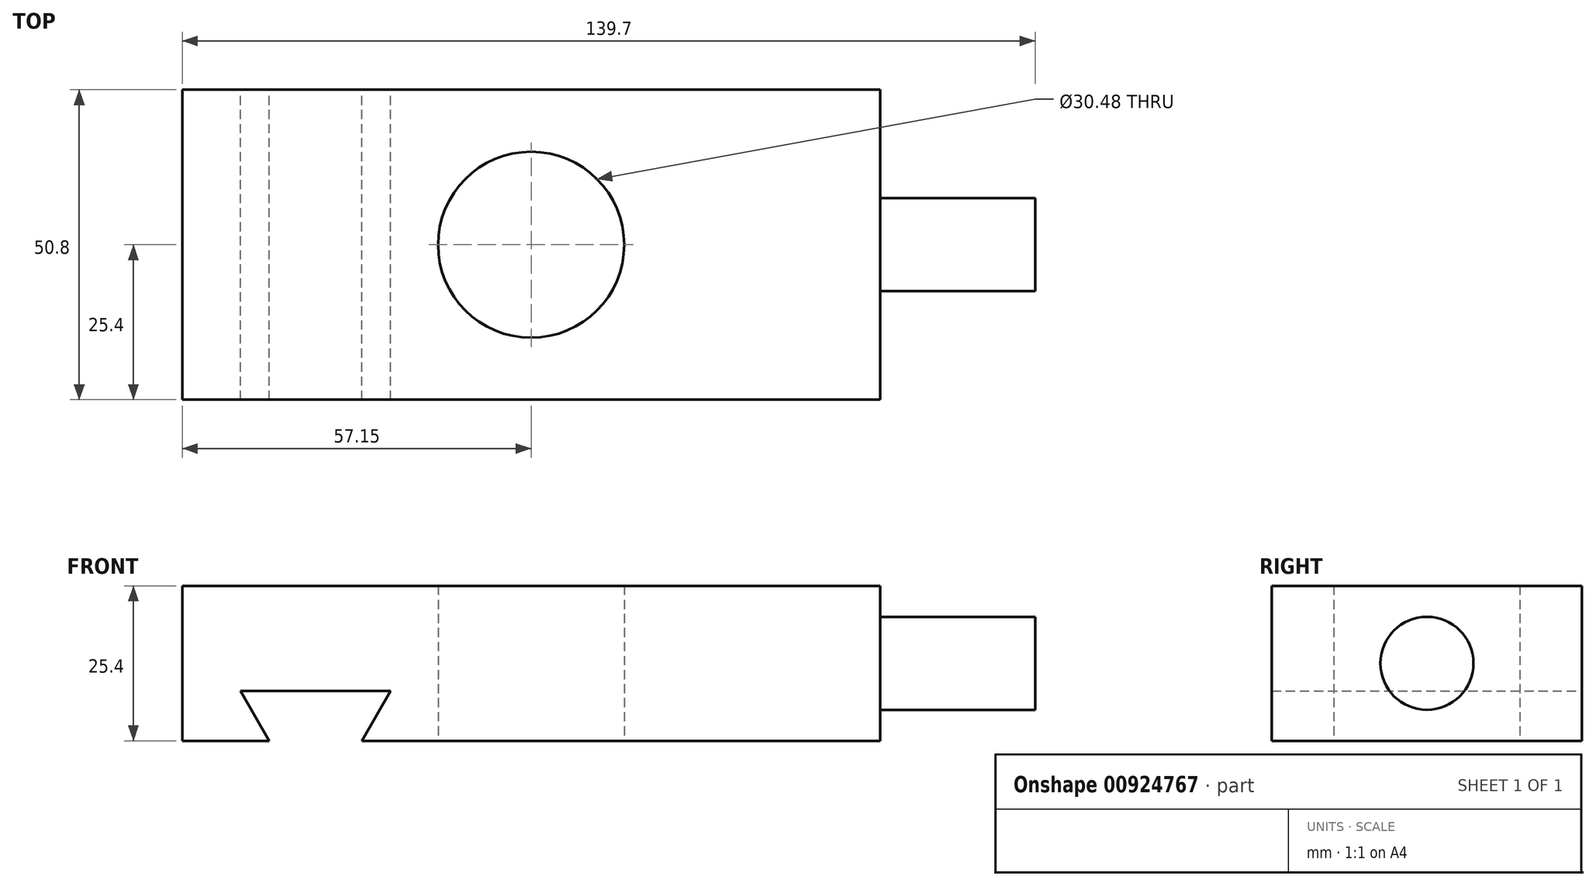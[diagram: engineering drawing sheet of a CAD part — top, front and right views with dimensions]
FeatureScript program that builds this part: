
annotation { "Feature Type Name" : "Feature", "Feature Type Description" : "" }
export const myFeature = defineFeature(function(context is Context, id is Id, definition is map)
    precondition{}
    {
        {
            var Q0;
            Q0=qCreatedBy(makeId("Top.planeOp"),FACE);
            var sketch = newSketch(context, id + "F0", { "sketchPlane" : qUnion([Q0])});
            skLineSegment(sketch, "E0.bottom", {"start": v(57.15, -25.4) * mm, "end": v(-57.15, -25.4) * mm});
            skLineSegment(sketch, "E0.top", {"start": v(57.15, 25.4) * mm, "end": v(-57.15, 25.4) * mm});
            skLineSegment(sketch, "E0.left", {"start": v(57.15, -25.4) * mm, "end": v(57.15, 25.4) * mm});
            skLineSegment(sketch, "E0.right", {"start": v(-57.15, -25.4) * mm, "end": v(-57.15, 25.4) * mm});
            skPoint(sketch, "E0.middle", {"position": v(0, 0) * mm});
            skCircle(sketch, "E1", {"center": v(0, 0) * mm, "radius": 15.24 * mm});
            skSolve(sketch);
        }
        {
            var Q0;
            Q0=makeQuery(id+"F0.imprint","IMPRINT",FACE,{"disambiguationData":[TD([[makeQuery(id+"F0.imprint","IMPRINT",EDGE,{"derivedFrom":sQuery(id+"F0.wireOp",EDGE,"E0.bottom")}),-1.0]])]});
            extrude(context, id + "F1", {"entities" : qUnion([Q0]), "depth" : 25.4 * mm, "offsetDistance" : 25.4 * mm});
        }
        {
            var Q0;
            Q0=makeQuery(id+"F1.opExtrude","CAP_FACE",FACE,{"disambiguationData":[OSD([sQuery(id+"F0.wireOp",EDGE,"E0.bottom"),sQuery(id+"F0.wireOp",EDGE,"E0.top"),sQuery(id+"F0.wireOp",EDGE,"E0.left"),sQuery(id+"F0.wireOp",EDGE,"E0.right"),sQuery(id+"F0.wireOp",EDGE,"E1")])],"isStart":false});
            var sketch = newSketch(context, id + "F2", { "sketchPlane" : qUnion([Q0])});
            skLineSegment(sketch, "E2.bottom", {"start": v(-42.93, 25.4) * mm, "end": v(-30.23, 25.4) * mm});
            skLineSegment(sketch, "E2.top", {"start": v(-42.93, -25.4) * mm, "end": v(-30.23, -25.4) * mm});
            skLineSegment(sketch, "E2.left", {"start": v(-42.93, 25.4) * mm, "end": v(-42.93, -25.4) * mm});
            skLineSegment(sketch, "E2.right", {"start": v(-30.23, 25.4) * mm, "end": v(-30.23, -25.4) * mm});
            skLineSegment(sketch, "E3.bottom", {"start": v(30.23, 25.4) * mm, "end": v(42.93, 25.4) * mm});
            skLineSegment(sketch, "E3.top", {"start": v(30.23, -25.4) * mm, "end": v(42.93, -25.4) * mm});
            skLineSegment(sketch, "E3.left", {"start": v(30.23, 25.4) * mm, "end": v(30.23, -25.4) * mm});
            skLineSegment(sketch, "E3.right", {"start": v(42.93, 25.4) * mm, "end": v(42.93, -25.4) * mm});
            skLineSegment(sketch, "E4", {"start": v(-25.15, 25.4) * mm, "end": v(-25.15, -25.4) * mm});
            skLineSegment(sketch, "E5", {"start": v(-17.53, 25.4) * mm, "end": v(-17.53, -25.4) * mm});
            skLineSegment(sketch, "E6", {"start": v(17.53, 25.4) * mm, "end": v(17.53, -25.4) * mm});
            skLineSegment(sketch, "E7", {"start": v(25.15, 25.4) * mm, "end": v(25.15, -25.4) * mm});
            skLineSegment(sketch, "E8", {"start": v(-3.81, 25.4) * mm, "end": v(-3.8, -25.4) * mm});
            skPoint(sketch, "E8.endSnap0", {"position": v(0, -25.4) * mm});
            skLineSegment(sketch, "E9", {"start": v(3.8, 25.4) * mm, "end": v(3.81, -25.4) * mm});
            skSolve(sketch);
        }
        {
            var Q0;
            Q0=makeQuery(id+"F1.opExtrude","SWEPT_FACE",FACE,{"disambiguationData":[OSD([sQuery(id+"F0.wireOp",EDGE,"E0.top")])]});
            var sketch = newSketch(context, id + "F3", { "sketchPlane" : qUnion([Q0])});
            skLineSegment(sketch, "E10", {"start": v(42.9, 0) * mm, "end": v(47.62, 8.17) * mm});
            skLineSegment(sketch, "E11", {"start": v(48.64, 8.17) * mm, "end": v(23.02, 8.17) * mm});
            skLineSegment(sketch, "E12", {"start": v(23.02, 8.17) * mm, "end": v(27.74, 0) * mm});
            skLineSegment(sketch, "E13", {"start": v(27.74, 0) * mm, "end": v(42.9, 0) * mm});
            skSolve(sketch);
        }
        {
            var Q0;
            {var subQ0=sQuery(id+"F3.wireOp",EDGE,"E10");Q0=makeQuery(id+"F3.imprint","IMPRINT",FACE,{"disambiguationData":[TD([[makeQuery(id+"F3.imprint","IMPRINT",EDGE,{"derivedFrom":subQ0}),1.0]])]});}
            extrude(context, id + "F4", {"entities" : qUnion([Q0]), "operationType" : NewBodyOperationType.REMOVE, "endBound" : BoundingType.THROUGH_ALL, "oppositeDirection" : true, "depth" : 25.4 * mm, "offsetDistance" : 25.4 * mm});
        }
        {
            var Q0;
            Q0=makeQuery(id+"F1.opExtrude","SWEPT_FACE",FACE,{"disambiguationData":[OSD([sQuery(id+"F0.wireOp",EDGE,"E0.left")])]});
            var sketch = newSketch(context, id + "F5", { "sketchPlane" : qUnion([Q0])});
            skPoint(sketch, "E14", {"position": v(0, 12.7) * mm});
            skPoint(sketch, "E14.positionSnap0", {"position": v(25.4, 12.7) * mm});
            skCircle(sketch, "E15", {"center": v(0, 12.7) * mm, "radius": 7.62 * mm});
            skSolve(sketch);
        }
        {
            var Q0;
            Q0=makeQuery(id+"F5.imprint","IMPRINT",FACE,{"disambiguationData":[TD([[makeQuery(id+"F5.imprint","IMPRINT",EDGE,{"derivedFrom":sQuery(id+"F5.wireOp",EDGE,"E15")}),1.0]])]});
            extrude(context, id + "F6", {"entities" : qUnion([Q0]), "operationType" : NewBodyOperationType.ADD, "depth" : 25.4 * mm, "offsetDistance" : 25.4 * mm});
        }
    });
